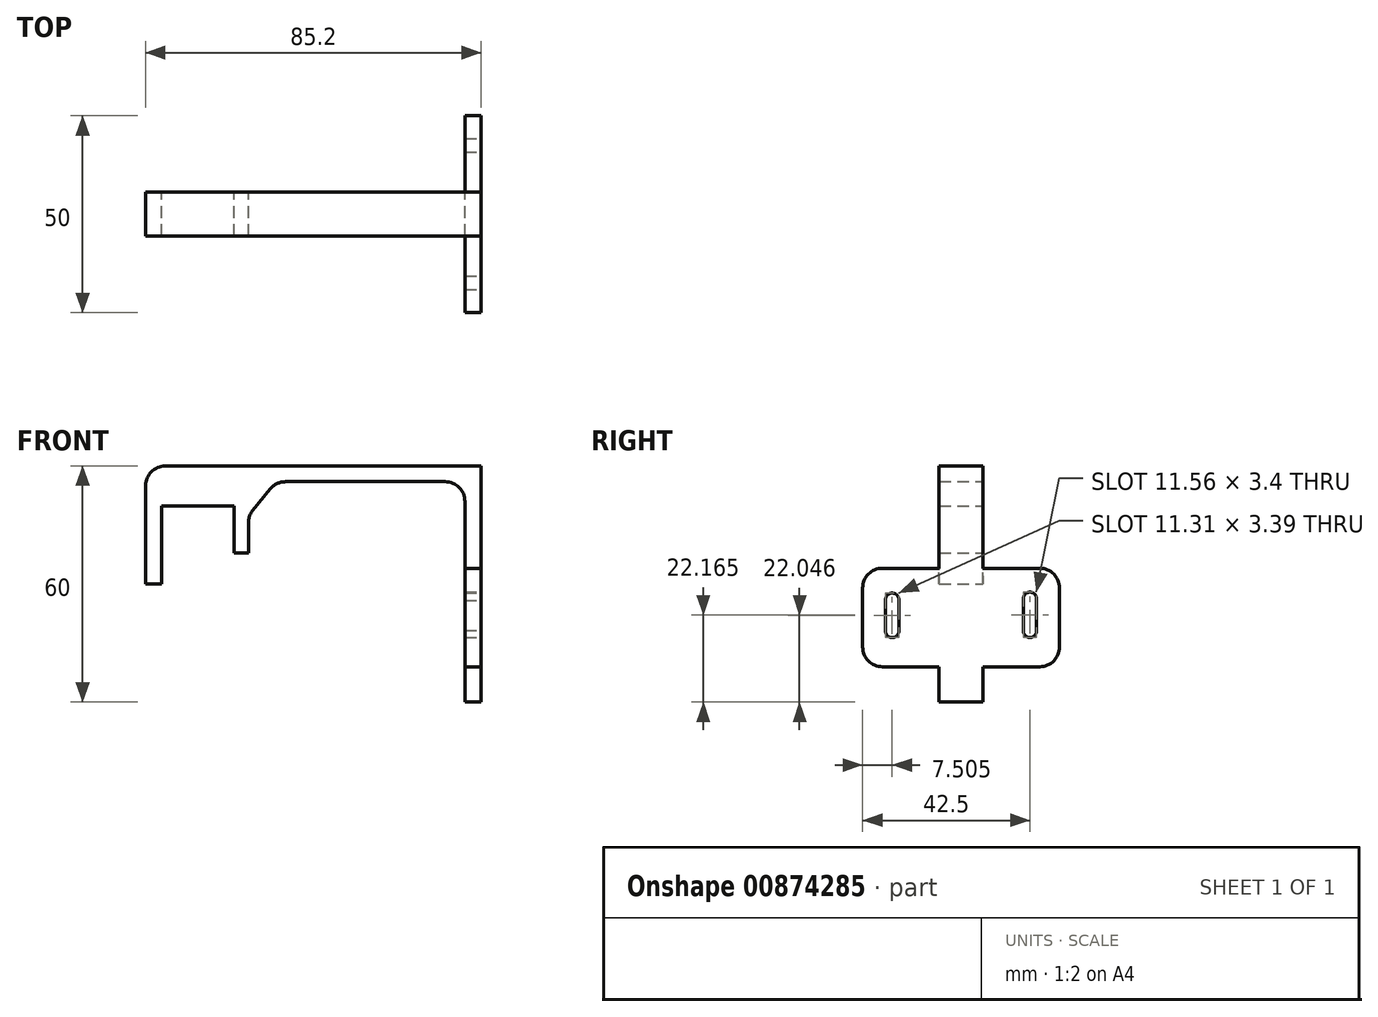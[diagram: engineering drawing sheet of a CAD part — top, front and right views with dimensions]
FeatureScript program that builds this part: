
annotation { "Feature Type Name" : "Feature", "Feature Type Description" : "" }
export const myFeature = defineFeature(function(context is Context, id is Id, definition is map)
    precondition{}
    {
        {
            var Q0;
            Q0=qCreatedBy(makeId("Front.planeOp"),FACE);
            var sketch = newSketch(context, id + "F0", { "sketchPlane" : qUnion([Q0])});
            skLineSegment(sketch, "E0", {"start": v(-53.8, 53.65) * mm, "end": v(-53.8, 28.65) * mm});
            skLineSegment(sketch, "E1", {"start": v(-53.8, 28.65) * mm, "end": v(-49.8, 28.65) * mm});
            skLineSegment(sketch, "E2", {"start": v(-49.8, 28.65) * mm, "end": v(-49.8, 48.5) * mm});
            skLineSegment(sketch, "E3", {"start": v(-49.8, 48.5) * mm, "end": v(-31.3, 48.5) * mm});
            skLineSegment(sketch, "E4", {"start": v(-31.3, 48.5) * mm, "end": v(-31.3, 36.5) * mm});
            skLineSegment(sketch, "E5", {"start": v(-27.7, 36.5) * mm, "end": v(-27.7, 44.22) * mm});
            skLineSegment(sketch, "E6", {"start": v(-26.57, 47.37) * mm, "end": v(-22.16, 52.8) * mm});
            skLineSegment(sketch, "E7", {"start": v(-18.28, 54.65) * mm, "end": v(22.3, 54.65) * mm});
            skLineSegment(sketch, "E8", {"start": v(27.3, 49.65) * mm, "end": v(27.3, -1.35) * mm});
            skLineSegment(sketch, "E9", {"start": v(31.4, -1.35) * mm, "end": v(31.4, 58.65) * mm});
            skLineSegment(sketch, "E10", {"start": v(26.37, 58.65) * mm, "end": v(-48.8, 58.65) * mm});
            skPoint(sketch, "E11.visualSharp", {"position": v(-53.8, 58.65) * mm});
            skArc(sketch, "E11.filletArc", {"start": v(-48.8, 58.65) * mm, "mid": v(-52.33, 57.19) * mm, "end": v(-53.8, 53.65) * mm});
            skPoint(sketch, "E12.visualSharp", {"position": v(-20.66, 54.65) * mm});
            skArc(sketch, "E12.filletArc", {"start": v(-18.28, 54.65) * mm, "mid": v(-20.43, 54.17) * mm, "end": v(-22.16, 52.8) * mm});
            skPoint(sketch, "E13.visualSharp", {"position": v(-27.7, 45.99) * mm});
            skArc(sketch, "E13.filletArc", {"start": v(-26.57, 47.37) * mm, "mid": v(-27.4, 45.89) * mm, "end": v(-27.7, 44.22) * mm});
            skPoint(sketch, "E14.visualSharp", {"position": v(27.3, 54.65) * mm});
            skArc(sketch, "E14.filletArc", {"start": v(27.3, 49.65) * mm, "mid": v(25.84, 53.19) * mm, "end": v(22.3, 54.65) * mm});
            skPoint(sketch, "E15.visualSharp", {"position": v(26.4, 58.65) * mm});
            skArc(sketch, "E15.filletArc", {"start": v(26.37, 58.65) * mm, "mid": v(26.39, 58.65) * mm, "end": v(26.4, 58.65) * mm});
            skLineSegment(sketch, "E16", {"start": v(-31.3, 36.5) * mm, "end": v(-27.7, 36.5) * mm});
            skPoint(sketch, "E17.end.orphan", {"position": v(27.3, 76.05) * mm});
            skLineSegment(sketch, "E18", {"start": v(26.4, 58.65) * mm, "end": v(31.4, 58.65) * mm});
            skLineSegment(sketch, "E19", {"start": v(31.4, -1.35) * mm, "end": v(27.3, -1.35) * mm});
            skPoint(sketch, "E20.orphan", {"position": v(23.22, -1.35) * mm});
            skSolve(sketch);
        }
        {
            var Q0;
            Q0=makeQuery(id+"F0.imprint","IMPRINT",FACE,{"disambiguationData":[TD([[makeQuery(id+"F0.imprint","IMPRINT",EDGE,{"derivedFrom":sQuery(id+"F0.wireOp",EDGE,"E0")}),1.0]])]});
            extrude(context, id + "F1", {"entities" : qUnion([Q0]), "depth" : 11.1 * mm, "offsetDistance" : 25 * mm});
        }
        {
            var Q0;
            Q0=makeQuery(id+"F1.opExtrude","SWEPT_FACE",FACE,{"disambiguationData":[OSD([sQuery(id+"F0.wireOp",EDGE,"E9")])]});
            var sketch = newSketch(context, id + "F2", { "sketchPlane" : qUnion([Q0])});
            skLineSegment(sketch, "E21.bottom", {"start": v(14.45, 7.65) * mm, "end": v(-25.55, 7.65) * mm});
            skLineSegment(sketch, "E21.top", {"start": v(14.45, 32.65) * mm, "end": v(-25.55, 32.65) * mm});
            skLineSegment(sketch, "E21.left", {"start": v(19.45, 12.65) * mm, "end": v(19.45, 27.65) * mm});
            skLineSegment(sketch, "E21.right", {"start": v(-30.55, 12.65) * mm, "end": v(-30.55, 27.65) * mm});
            skPoint(sketch, "E21.middle", {"position": v(-5.55, 20.15) * mm});
            skPoint(sketch, "E21.middle.positionSnap0", {"position": v(-5.55, -1.35) * mm});
            skPoint(sketch, "E21.centerSnap0", {"position": v(-5.55, -1.35) * mm});
            skArc(sketch, "E22", {"start": v(-21.35, 24.65) * mm, "mid": v(-23.14, 26.35) * mm, "end": v(-24.74, 24.47) * mm});
            skLineSegment(sketch, "E23", {"start": v(-23.05, 49.86) * mm, "end": v(-23.05, -0.25) * mm, "construction": true});
            skLineSegment(sketch, "E24", {"start": v(11.95, 54.3) * mm, "end": v(11.95, 0) * mm, "construction": true});
            skArc(sketch, "E25", {"start": v(-24.74, 16.92) * mm, "mid": v(-23.14, 15.04) * mm, "end": v(-21.35, 16.74) * mm});
            skArc(sketch, "E26", {"start": v(13.65, 24.9) * mm, "mid": v(11.95, 26.6) * mm, "end": v(10.25, 24.9) * mm});
            skArc(sketch, "E27", {"start": v(10.25, 16.73) * mm, "mid": v(11.95, 15.03) * mm, "end": v(13.65, 16.73) * mm});
            skLineSegment(sketch, "E28", {"start": v(-21.35, 24.65) * mm, "end": v(-21.35, 16.74) * mm});
            skLineSegment(sketch, "E29", {"start": v(-24.74, 24.84) * mm, "end": v(-24.74, 16.55) * mm});
            skLineSegment(sketch, "E30", {"start": v(10.25, 24.9) * mm, "end": v(10.25, 16.73) * mm});
            skLineSegment(sketch, "E31", {"start": v(13.65, 24.9) * mm, "end": v(13.65, 16.73) * mm});
            skLineSegment(sketch, "E32", {"start": v(-23.05, 24.65) * mm, "end": v(35.7, 24.65) * mm, "construction": true});
            skLineSegment(sketch, "E33", {"start": v(-10.11, 58.65) * mm, "end": v(23.75, 58.65) * mm, "construction": true});
            skPoint(sketch, "E34.visualSharp", {"position": v(-30.55, 32.65) * mm});
            skArc(sketch, "E34.filletArc", {"start": v(-25.55, 32.65) * mm, "mid": v(-29.09, 31.19) * mm, "end": v(-30.55, 27.65) * mm});
            skPoint(sketch, "E35.visualSharp", {"position": v(19.45, 32.65) * mm});
            skArc(sketch, "E35.filletArc", {"start": v(19.45, 27.65) * mm, "mid": v(17.99, 31.19) * mm, "end": v(14.45, 32.65) * mm});
            skPoint(sketch, "E36.visualSharp", {"position": v(19.45, 7.65) * mm});
            skArc(sketch, "E36.filletArc", {"start": v(14.45, 7.65) * mm, "mid": v(17.99, 9.12) * mm, "end": v(19.45, 12.65) * mm});
            skPoint(sketch, "E37.visualSharp", {"position": v(-30.55, 7.65) * mm});
            skArc(sketch, "E37.filletArc", {"start": v(-30.55, 12.65) * mm, "mid": v(-29.09, 9.12) * mm, "end": v(-25.55, 7.65) * mm});
            skSolve(sketch);
        }
        {
            var Q0;
            Q0=makeQuery(id+"F2.imprint","IMPRINT",FACE,{"disambiguationData":[TD([[makeQuery(id+"F2.imprint","IMPRINT",EDGE,{"derivedFrom":sQuery(id+"F2.wireOp",EDGE,"E21.left")}),1.0]])]});
            var Q1;
            Q1=makeQuery(id+"F2.imprint","IMPRINT",FACE,{"disambiguationData":[TD([[makeQuery(id+"F2.imprint","IMPRINT",EDGE,{"derivedFrom":sQuery(id+"F2.wireOp",EDGE,"E21.right")}),-1.0]])]});
            extrude(context, id + "F3", {"entities" : qUnion([Q0, Q1]), "operationType" : NewBodyOperationType.ADD, "oppositeDirection" : true, "depth" : 4.1 * mm, "offsetDistance" : 25 * mm});
        }
    });
